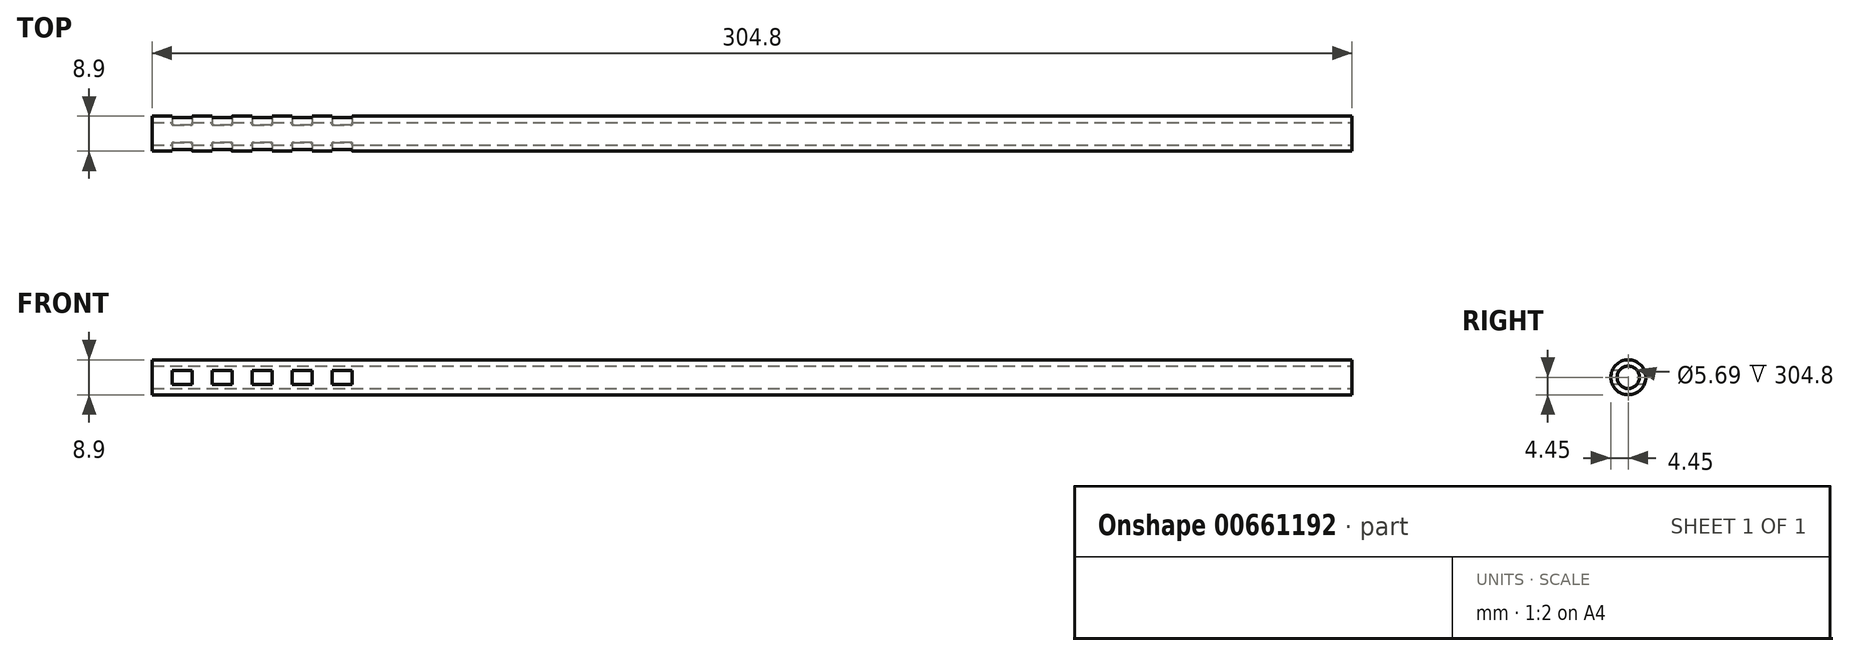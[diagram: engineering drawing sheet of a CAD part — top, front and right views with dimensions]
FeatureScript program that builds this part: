
annotation { "Feature Type Name" : "Feature", "Feature Type Description" : "" }
export const myFeature = defineFeature(function(context is Context, id is Id, definition is map)
    precondition{}
    {
        {
            var Q0;
            Q0=qCreatedBy(makeId("Right.planeOp"),FACE);
            var sketch = newSketch(context, id + "F0", { "sketchPlane" : qUnion([Q0])});
            skCircle(sketch, "E0", {"center": v(0, 0) * mm, "radius": 4.45 * mm});
            skCircle(sketch, "E1", {"center": v(0, 0) * mm, "radius": 2.84 * mm});
            skSolve(sketch);
        }
        {
            var Q0;
            Q0=makeQuery(id+"F0.imprint","IMPRINT",FACE,{"disambiguationData":[TD([[makeQuery(id+"F0.imprint","IMPRINT",EDGE,{"derivedFrom":sQuery(id+"F0.wireOp",EDGE,"E0")}),1.0]])]});
            extrude(context, id + "F1", {"entities" : qUnion([Q0]), "oppositeDirection" : true, "depth" : 12.7 * mm, "offsetDistance" : 25.4 * mm});
        }
        {
            var Q0;
            Q0=makeQuery(id+"F0.imprint","IMPRINT",FACE,{"disambiguationData":[TD([[makeQuery(id+"F0.imprint","IMPRINT",EDGE,{"derivedFrom":sQuery(id+"F0.wireOp",EDGE,"E0")}),1.0]])]});
            extrude(context, id + "F2", {"entities" : qUnion([Q0]), "operationType" : NewBodyOperationType.ADD, "oppositeDirection" : true, "depth" : 304.8 * mm, "offsetDistance" : 25.4 * mm});
        }
        {
            var Q0;
            Q0=qCreatedBy(makeId("Front.planeOp"),FACE);
            var sketch = newSketch(context, id + "F3", { "sketchPlane" : qUnion([Q0])});
            skLineSegment(sketch, "E2", {"start": v(-304.8, 0.02) * mm, "end": v(-304.8, 1.8) * mm});
            skLineSegment(sketch, "E3", {"start": v(-304.8, 0.02) * mm, "end": v(-304.8, -1.76) * mm});
            skLineSegment(sketch, "E4", {"start": v(-304.8, -1.76) * mm, "end": v(-254, -1.8) * mm});
            skLineSegment(sketch, "E5", {"start": v(-254, -1.8) * mm, "end": v(-254, 1.76) * mm});
            skLineSegment(sketch, "E6", {"start": v(-254, 1.76) * mm, "end": v(-304.8, 1.8) * mm});
            skLineSegment(sketch, "E7", {"start": v(-259.08, 1.76) * mm, "end": v(-259.08, -1.8) * mm});
            skLineSegment(sketch, "E8", {"start": v(-264.16, 1.77) * mm, "end": v(-264.16, -1.79) * mm});
            skLineSegment(sketch, "E9", {"start": v(-269.24, 1.77) * mm, "end": v(-269.24, -1.79) * mm});
            skLineSegment(sketch, "E10", {"start": v(-274.32, 1.77) * mm, "end": v(-274.32, -1.78) * mm});
            skLineSegment(sketch, "E11", {"start": v(-279.4, 1.78) * mm, "end": v(-279.4, -1.78) * mm});
            skLineSegment(sketch, "E12", {"start": v(-284.48, 1.78) * mm, "end": v(-284.48, -1.78) * mm});
            skLineSegment(sketch, "E13", {"start": v(-289.56, 1.78) * mm, "end": v(-289.56, -1.77) * mm});
            skLineSegment(sketch, "E14", {"start": v(-294.64, 1.79) * mm, "end": v(-294.64, -1.77) * mm});
            skLineSegment(sketch, "E15", {"start": v(-299.72, 1.8) * mm, "end": v(-299.72, -1.76) * mm});
            skLineSegment(sketch, "E16", {"start": v(-254, -0.02) * mm, "end": v(-259.08, -0.01) * mm});
            skLineSegment(sketch, "E17", {"start": v(-259.08, -0.01) * mm, "end": v(-264.16, -0.01) * mm});
            skLineSegment(sketch, "E18", {"start": v(-264.16, -0.01) * mm, "end": v(-269.24, 0) * mm});
            skLineSegment(sketch, "E19", {"start": v(-269.24, 0) * mm, "end": v(-274.32, 0) * mm});
            skLineSegment(sketch, "E20", {"start": v(-274.32, 0) * mm, "end": v(-279.4, 0) * mm});
            skLineSegment(sketch, "E21", {"start": v(-279.4, 0) * mm, "end": v(-284.48, 0) * mm});
            skLineSegment(sketch, "E22", {"start": v(-284.48, 0) * mm, "end": v(-289.56, 0) * mm});
            skLineSegment(sketch, "E23", {"start": v(-289.56, 0) * mm, "end": v(-294.64, 0) * mm});
            skLineSegment(sketch, "E24", {"start": v(-299.72, 0.01) * mm, "end": v(-304.8, 0.02) * mm});
            skLineSegment(sketch, "E25", {"start": v(-294.64, 0) * mm, "end": v(-299.72, 0.01) * mm});
            skSolve(sketch);
        }
        {
            var Q0;
            {var subQ5=sQuery(id+"F3.wireOp",EDGE,"E16");Q0=makeQuery(id+"F3.imprint","IMPRINT",FACE,{"disambiguationData":[TD([[makeQuery(id+"F3.imprint","IMPRINT",EDGE,{"derivedFrom":subQ5}),1.0]])]});}
            var Q1;
            {var subQ3=sQuery(id+"F3.wireOp",EDGE,"E16");Q1=makeQuery(id+"F3.imprint","IMPRINT",FACE,{"disambiguationData":[TD([[makeQuery(id+"F3.imprint","IMPRINT",EDGE,{"derivedFrom":subQ3}),-1.0]])]});}
            var Q2;
            {var subQ5=sQuery(id+"F3.wireOp",EDGE,"E18");Q2=makeQuery(id+"F3.imprint","IMPRINT",FACE,{"disambiguationData":[TD([[makeQuery(id+"F3.imprint","IMPRINT",EDGE,{"derivedFrom":subQ5}),-1.0]])]});}
            var Q3;
            {var subQ5=sQuery(id+"F3.wireOp",EDGE,"E18");Q3=makeQuery(id+"F3.imprint","IMPRINT",FACE,{"disambiguationData":[TD([[makeQuery(id+"F3.imprint","IMPRINT",EDGE,{"derivedFrom":subQ5}),1.0]])]});}
            var Q4;
            {var subQ5=sQuery(id+"F3.wireOp",EDGE,"E20");Q4=makeQuery(id+"F3.imprint","IMPRINT",FACE,{"disambiguationData":[TD([[makeQuery(id+"F3.imprint","IMPRINT",EDGE,{"derivedFrom":subQ5}),-1.0]])]});}
            var Q5;
            {var subQ5=sQuery(id+"F3.wireOp",EDGE,"E20");Q5=makeQuery(id+"F3.imprint","IMPRINT",FACE,{"disambiguationData":[TD([[makeQuery(id+"F3.imprint","IMPRINT",EDGE,{"derivedFrom":subQ5}),1.0]])]});}
            var Q6;
            {var subQ5=sQuery(id+"F3.wireOp",EDGE,"E22");Q6=makeQuery(id+"F3.imprint","IMPRINT",FACE,{"disambiguationData":[TD([[makeQuery(id+"F3.imprint","IMPRINT",EDGE,{"derivedFrom":subQ5}),1.0]])]});}
            var Q7;
            {var subQ5=sQuery(id+"F3.wireOp",EDGE,"E22");Q7=makeQuery(id+"F3.imprint","IMPRINT",FACE,{"disambiguationData":[TD([[makeQuery(id+"F3.imprint","IMPRINT",EDGE,{"derivedFrom":subQ5}),-1.0]])]});}
            var Q8;
            {var subQ5=sQuery(id+"F3.wireOp",EDGE,"E25");Q8=makeQuery(id+"F3.imprint","IMPRINT",FACE,{"disambiguationData":[TD([[makeQuery(id+"F3.imprint","IMPRINT",EDGE,{"derivedFrom":subQ5}),1.0]])]});}
            var Q9;
            {var subQ5=sQuery(id+"F3.wireOp",EDGE,"E25");Q9=makeQuery(id+"F3.imprint","IMPRINT",FACE,{"disambiguationData":[TD([[makeQuery(id+"F3.imprint","IMPRINT",EDGE,{"derivedFrom":subQ5}),-1.0]])]});}
            extrude(context, id + "F4", {"entities" : qUnion([Q0, Q1, Q2, Q3, Q4, Q5, Q6, Q7, Q8, Q9]), "operationType" : NewBodyOperationType.REMOVE, "oppositeDirection" : true, "depth" : 25.4 * mm, "offsetDistance" : 25.4 * mm, "hasSecondDirection" : true, "secondDirectionOppositeDirection" : false, "secondDirectionDepth" : 25.4 * mm});
        }
    });
